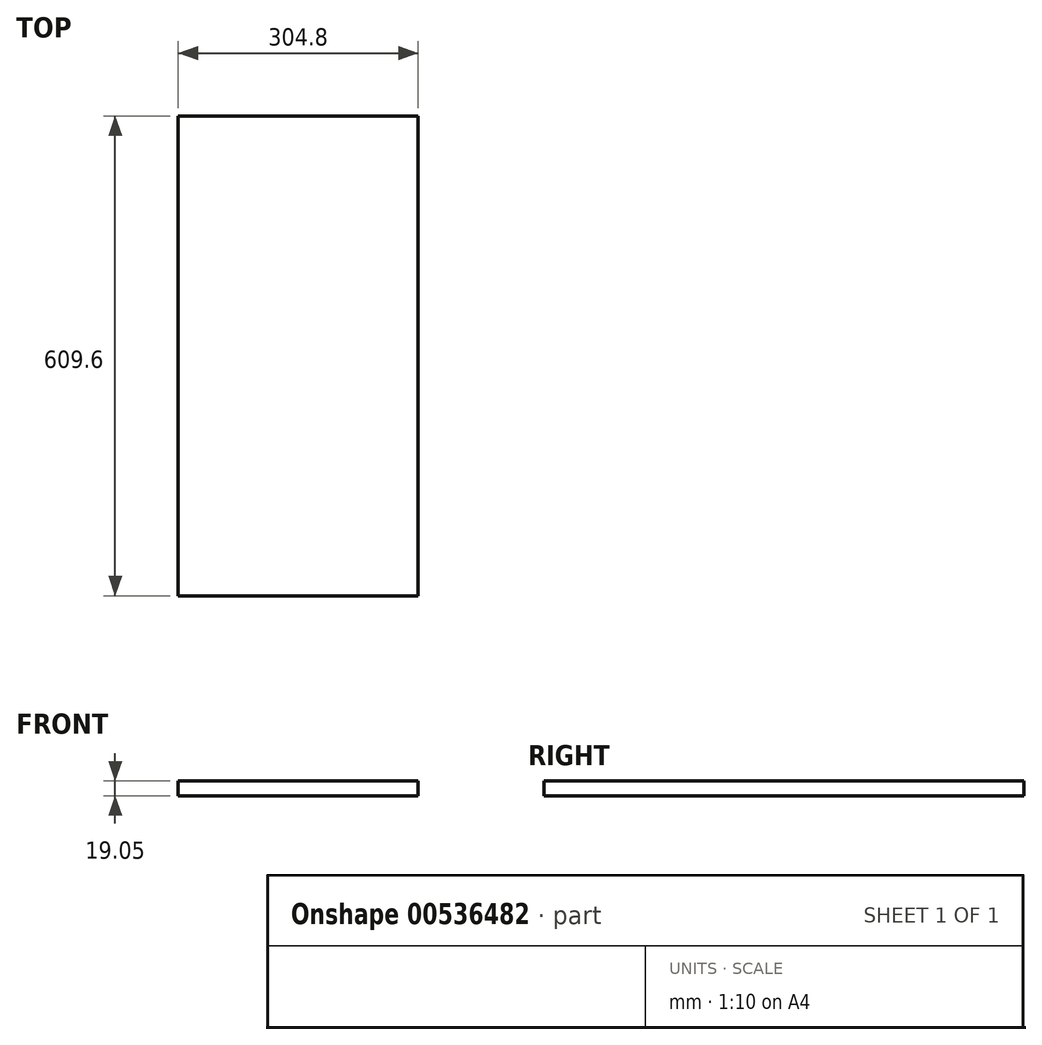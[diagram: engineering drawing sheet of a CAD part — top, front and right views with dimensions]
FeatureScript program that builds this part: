
annotation { "Feature Type Name" : "Feature", "Feature Type Description" : "" }
export const myFeature = defineFeature(function(context is Context, id is Id, definition is map)
    precondition{}
    {
        {
            var Q0;
            Q0=qCreatedBy(makeId("Top.planeOp"),FACE);
            var sketch = newSketch(context, id + "F0", { "sketchPlane" : qUnion([Q0])});
            skLineSegment(sketch, "E0.bottom", {"start": v(0, 0) * mm, "end": v(304.8, 0) * mm});
            skLineSegment(sketch, "E0.top", {"start": v(0, -609.6) * mm, "end": v(304.8, -609.6) * mm});
            skLineSegment(sketch, "E0.left", {"start": v(0, 0) * mm, "end": v(0, -609.6) * mm});
            skLineSegment(sketch, "E0.right", {"start": v(304.8, 0) * mm, "end": v(304.8, -609.6) * mm});
            skSolve(sketch);
        }
        {
            var Q0;
            Q0=makeQuery(id+"F0.imprint","IMPRINT",FACE,{"disambiguationData":[TD([[makeQuery(id+"F0.imprint","IMPRINT",EDGE,{"derivedFrom":sQuery(id+"F0.wireOp",EDGE,"E0.bottom")}),-1.0]])]});
            extrude(context, id + "F1", {"entities" : qUnion([Q0]), "depth" : 19.05 * mm, "offsetDistance" : 25.4 * mm});
        }
    });
